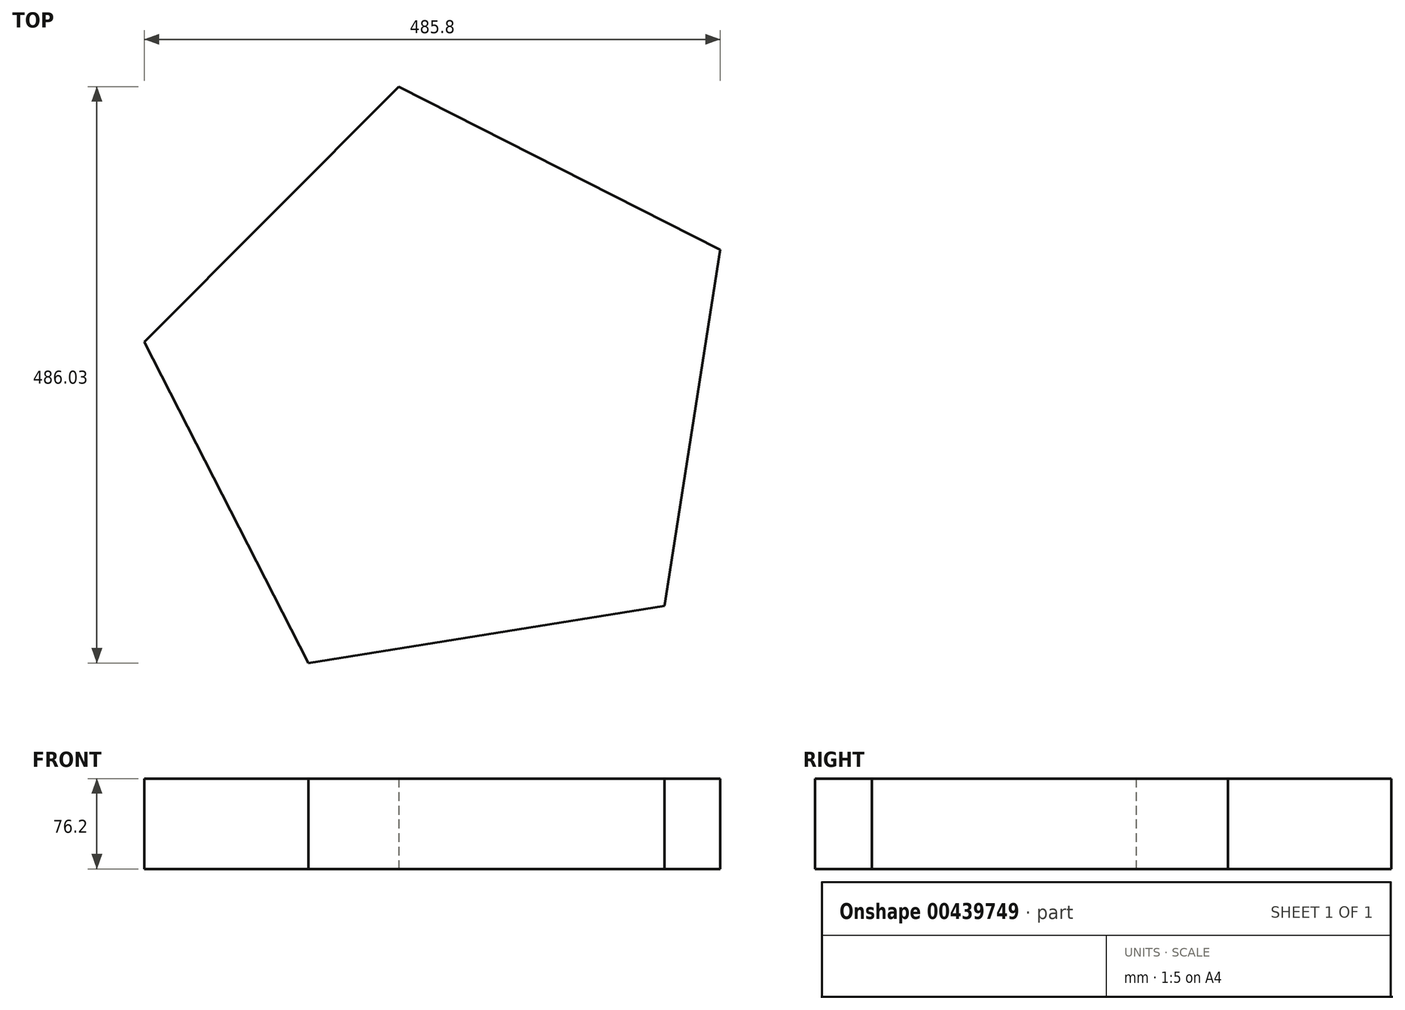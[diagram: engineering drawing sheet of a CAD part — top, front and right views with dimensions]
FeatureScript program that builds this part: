
annotation { "Feature Type Name" : "Feature", "Feature Type Description" : "" }
export const myFeature = defineFeature(function(context is Context, id is Id, definition is map)
    precondition{}
    {
        {
            var Q0;
            Q0=qCreatedBy(makeId("Top.planeOp"),FACE);
            var sketch = newSketch(context, id + "F0", { "sketchPlane" : qUnion([Q0])});
            skCircle(sketch, "E0.cCircle", {"center": v(0, 0) * mm, "radius": 209.25 * mm, "construction": true});
            skLineSegment(sketch, "E0.0", {"start": v(-255.52, 40.08) * mm, "end": v(-40.85, 255.4) * mm});
            skLineSegment(sketch, "E0.1", {"start": v(-40.85, 255.4) * mm, "end": v(230.28, 117.77) * mm});
            skLineSegment(sketch, "E0.2", {"start": v(230.28, 117.77) * mm, "end": v(183.16, -182.61) * mm});
            skLineSegment(sketch, "E0.3", {"start": v(183.16, -182.61) * mm, "end": v(-117.08, -230.63) * mm});
            skLineSegment(sketch, "E0.4", {"start": v(-117.08, -230.63) * mm, "end": v(-255.52, 40.08) * mm});
            skPoint(sketch, "E0.0.midPoint", {"position": v(-148.18, 147.74) * mm});
            skSolve(sketch);
        }
        {
            var Q0;
            Q0=makeQuery(id+"F0.imprint","IMPRINT",FACE,{"disambiguationData":[TD([[makeQuery(id+"F0.imprint","IMPRINT",EDGE,{"derivedFrom":sQuery(id+"F0.wireOp",EDGE,"E0.0")}),-1.0]])]});
            extrude(context, id + "F1", {"entities" : qUnion([Q0]), "depth" : 76.2 * mm});
        }
    });
